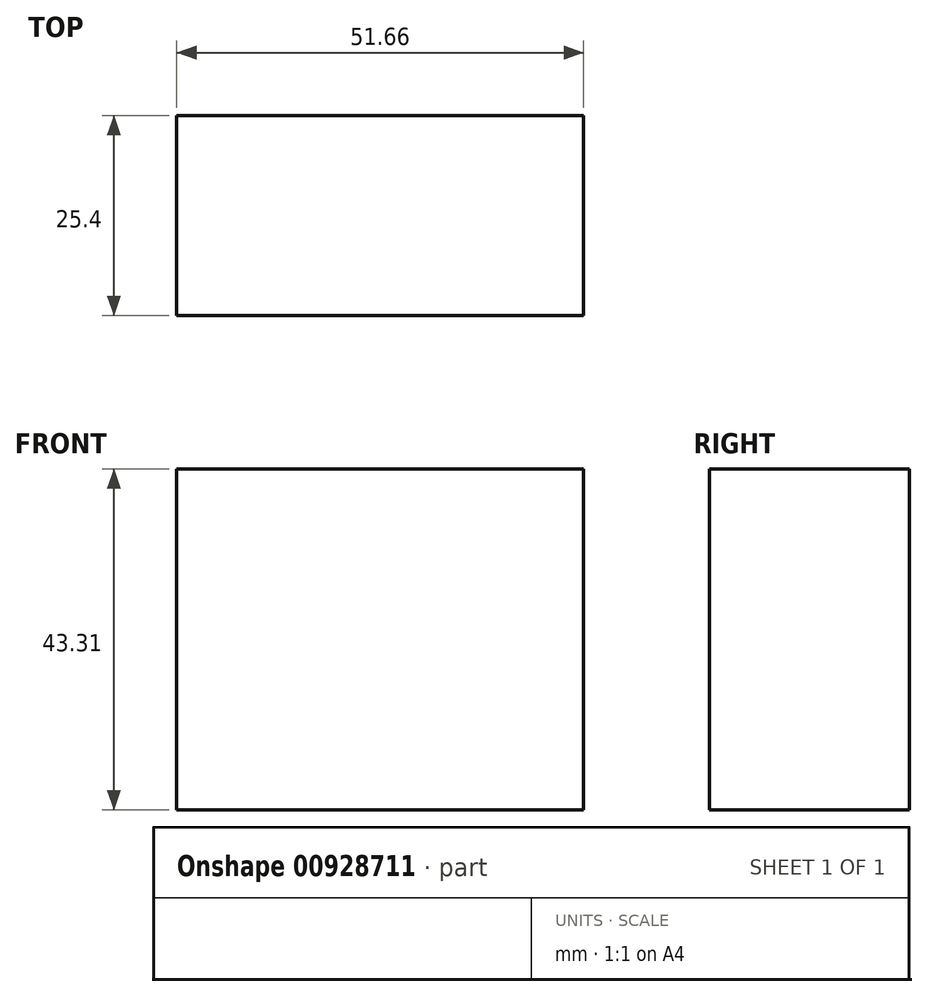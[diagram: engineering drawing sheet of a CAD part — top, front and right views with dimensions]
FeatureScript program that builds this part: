
annotation { "Feature Type Name" : "Feature", "Feature Type Description" : "" }
export const myFeature = defineFeature(function(context is Context, id is Id, definition is map)
    precondition{}
    {
        {
            var Q0;
            Q0=qCreatedBy(makeId("Front.planeOp"),FACE);
            var sketch = newSketch(context, id + "F0", { "sketchPlane" : qUnion([Q0])});
            skLineSegment(sketch, "E0.bottom", {"start": v(0, 0) * mm, "end": v(51.66, 0) * mm});
            skLineSegment(sketch, "E0.top", {"start": v(0, 43.3) * mm, "end": v(51.66, 43.3) * mm});
            skLineSegment(sketch, "E0.left", {"start": v(0, 0) * mm, "end": v(0, 43.3) * mm});
            skLineSegment(sketch, "E0.right", {"start": v(51.66, 0) * mm, "end": v(51.66, 43.3) * mm});
            skSolve(sketch);
        }
        {
            var Q0;
            Q0=makeQuery(id+"F0.imprint","IMPRINT",FACE,{"disambiguationData":[TD([[makeQuery(id+"F0.imprint","IMPRINT",EDGE,{"derivedFrom":sQuery(id+"F0.wireOp",EDGE,"E0.bottom")}),1.0]])]});
            extrude(context, id + "F1", {"entities" : qUnion([Q0]), "depth" : 25.4 * mm, "offsetDistance" : 25.4 * mm});
        }
    });
